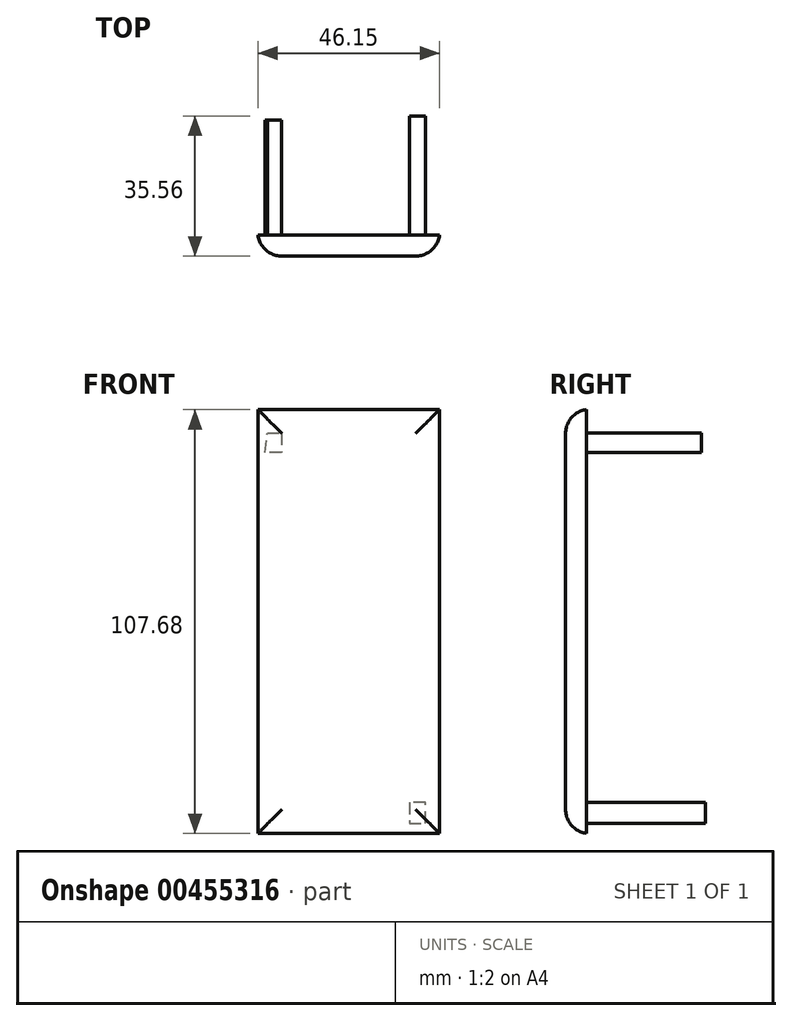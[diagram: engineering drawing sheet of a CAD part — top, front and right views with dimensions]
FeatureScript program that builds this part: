
annotation { "Feature Type Name" : "Feature", "Feature Type Description" : "" }
export const myFeature = defineFeature(function(context is Context, id is Id, definition is map)
    precondition{}
    {
        {
            var Q0;
            Q0=qCreatedBy(makeId("Front.planeOp"),FACE);
            var sketch = newSketch(context, id + "F0", { "sketchPlane" : qUnion([Q0])});
            skLineSegment(sketch, "E0.bottom", {"start": v(-31.2, 55.87) * mm, "end": v(14.96, 55.87) * mm});
            skLineSegment(sketch, "E0.top", {"start": v(-31.2, -51.8) * mm, "end": v(14.96, -51.8) * mm});
            skLineSegment(sketch, "E0.left", {"start": v(-31.2, 55.87) * mm, "end": v(-31.2, -51.8) * mm});
            skLineSegment(sketch, "E0.right", {"start": v(14.96, 55.87) * mm, "end": v(14.96, -51.8) * mm});
            skSolve(sketch);
        }
        {
            var Q0;
            Q0 = qSketchRegion(id + "F0", true);
            extrude(context, id + "F1", {"entities" : qUnion([Q0]), "depth" : 5.33 * mm});
        }
        {
            var Q0;
            Q0=makeQuery(id+"F1.opExtrude","CAP_FACE",FACE,{"disambiguationData":[OSD([sQuery(id+"F0.wireOp",EDGE,"E0.bottom"),sQuery(id+"F0.wireOp",EDGE,"E0.top"),sQuery(id+"F0.wireOp",EDGE,"E0.left"),sQuery(id+"F0.wireOp",EDGE,"E0.right")])],"isStart":false});
            fillet(context, id + "F2", {"entities" : qUnion([Q0]), "radius" : 6.13 * mm, "tangentPropagation" : true, "allowEdgeOverflow" : false});
        }
        {
            var Q0;
            Q0=qCreatedBy(makeId("Front.planeOp"),FACE);
            var sketch = newSketch(context, id + "F3", { "sketchPlane" : qUnion([Q0])});
            skLineSegment(sketch, "E1", {"start": v(12.96, 53.09) * mm, "end": v(8.08, 53.09) * mm});
            skLineSegment(sketch, "E2", {"start": v(8.08, 53.09) * mm, "end": v(8.08, 47.8) * mm});
            skLineSegment(sketch, "E3", {"start": v(8.08, 47.8) * mm, "end": v(12.62, 47.8) * mm});
            skLineSegment(sketch, "E4", {"start": v(12.62, 47.8) * mm, "end": v(12.96, 53.09) * mm});
            skSolve(sketch);
        }
        {
            var Q0;
            Q0=sQuery(id+"F3.wireOp",EDGE,"E1");
            var Q1;
            Q1=sQuery(id+"F3.wireOp",EDGE,"E4");
            var Q2;
            Q2=sQuery(id+"F3.wireOp",EDGE,"E3");
            var Q3;
            Q3=sQuery(id+"F3.wireOp",EDGE,"E2");
            extrude(context, id + "F4", {"bodyType" : ToolBodyType.SURFACE, "surfaceEntities" : qUnion([Q0, Q1, Q2, Q3]), "oppositeDirection" : true, "depth" : 26.42 * mm});
        }
        {
            var Q0;
            Q0=qCreatedBy(makeId("Front.planeOp"),FACE);
            var sketch = newSketch(context, id + "F5", { "sketchPlane" : qUnion([Q0])});
            skLineSegment(sketch, "E5", {"start": v(-28.81, 49.87) * mm, "end": v(-25.24, 49.87) * mm});
            skLineSegment(sketch, "E6", {"start": v(-25.24, 49.87) * mm, "end": v(-25.24, 44.97) * mm});
            skLineSegment(sketch, "E7", {"start": v(-25.24, 44.97) * mm, "end": v(-29.44, 44.97) * mm});
            skLineSegment(sketch, "E8", {"start": v(-29.44, 44.97) * mm, "end": v(-28.81, 49.87) * mm});
            skSolve(sketch);
        }
        {
            var Q0;
            Q0 = qSketchRegion(id + "F5", true);
            extrude(context, id + "F6", {"entities" : qUnion([Q0]), "operationType" : NewBodyOperationType.ADD, "oppositeDirection" : true, "depth" : 29.2 * mm});
        }
        {
            var Q0;
            Q0=qCreatedBy(makeId("Front.planeOp"),FACE);
            var sketch = newSketch(context, id + "F7", { "sketchPlane" : qUnion([Q0])});
            skLineSegment(sketch, "E9", {"start": v(11.36, -43.97) * mm, "end": v(7.28, -43.97) * mm});
            skLineSegment(sketch, "E10", {"start": v(7.28, -43.97) * mm, "end": v(7.28, -49.22) * mm});
            skLineSegment(sketch, "E11", {"start": v(7.28, -49.22) * mm, "end": v(11.35, -49.22) * mm});
            skLineSegment(sketch, "E12", {"start": v(11.35, -49.22) * mm, "end": v(11.36, -43.97) * mm});
            skSolve(sketch);
        }
        {
            var Q0;
            Q0=makeQuery(id+"F7.imprint","IMPRINT",FACE,{"disambiguationData":[TD([[makeQuery(id+"F7.imprint","IMPRINT",EDGE,{"derivedFrom":sQuery(id+"F7.wireOp",EDGE,"E9")}),1.0]])]});
            extrude(context, id + "F8", {"entities" : qUnion([Q0]), "operationType" : NewBodyOperationType.ADD, "oppositeDirection" : true, "depth" : 30.23 * mm});
        }
    });
